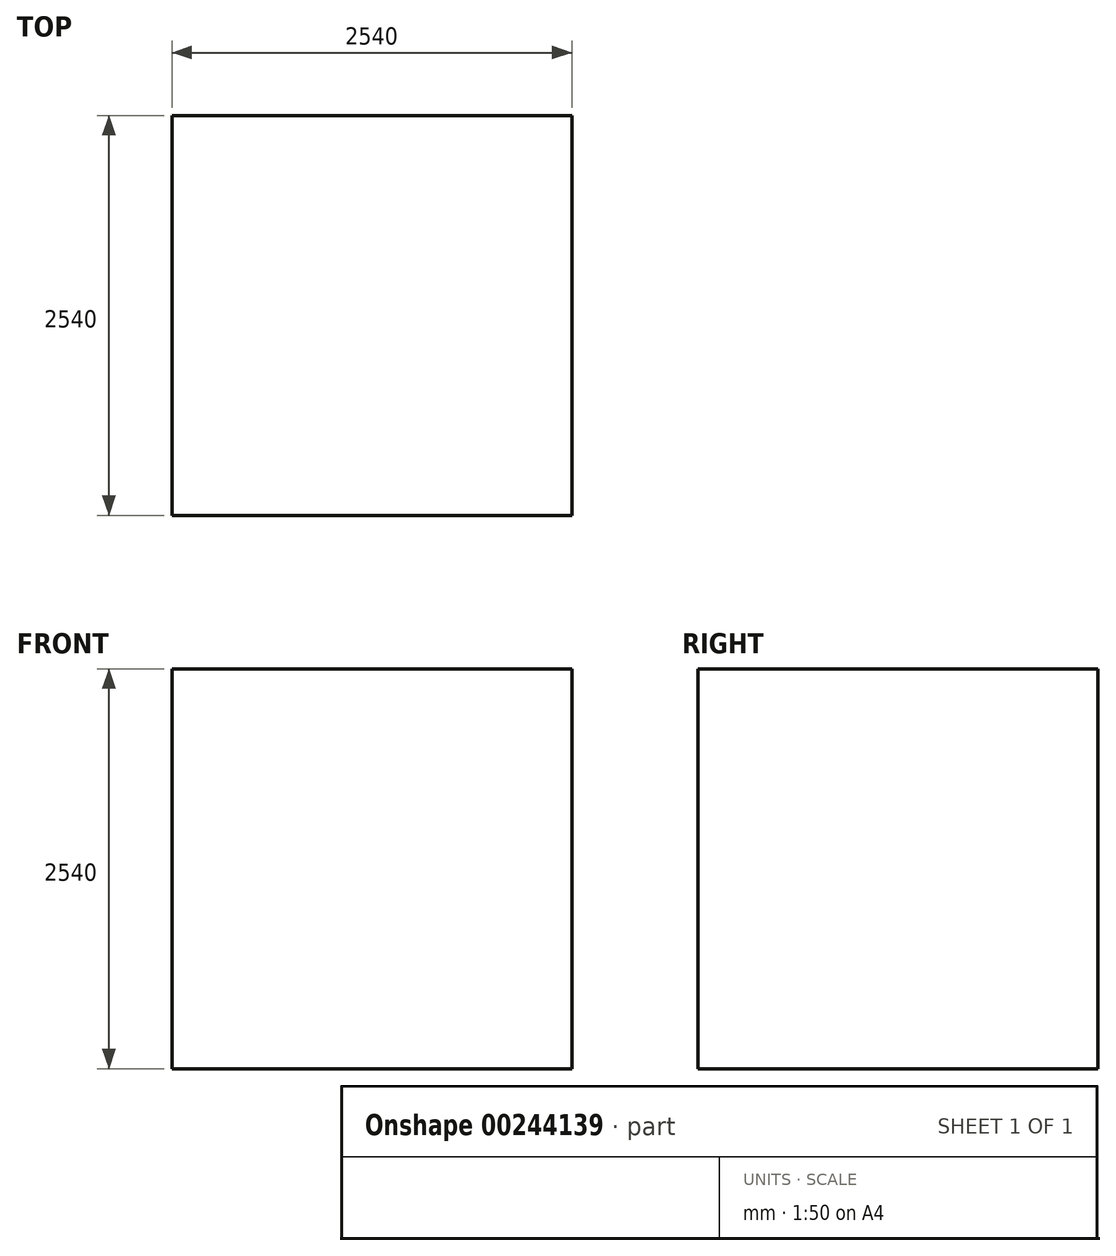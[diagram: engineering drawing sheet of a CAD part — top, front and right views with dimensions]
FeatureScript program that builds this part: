
annotation { "Feature Type Name" : "Feature", "Feature Type Description" : "" }
export const myFeature = defineFeature(function(context is Context, id is Id, definition is map)
    precondition{}
    {
        {
            var Q0;
            Q0=qCreatedBy(makeId("Top.planeOp"),FACE);
            var sketch = newSketch(context, id + "F0", { "sketchPlane" : qUnion([Q0])});
            skLineSegment(sketch, "E0.bottom", {"start": v(-1270.15, 1260.76) * mm, "end": v(1269.85, 1260.76) * mm});
            skLineSegment(sketch, "E0.top", {"start": v(-1270.15, -1279.24) * mm, "end": v(1269.85, -1279.24) * mm});
            skLineSegment(sketch, "E0.left", {"start": v(-1270.15, 1260.76) * mm, "end": v(-1270.15, -1279.24) * mm});
            skLineSegment(sketch, "E0.right", {"start": v(1269.85, 1260.76) * mm, "end": v(1269.85, -1279.24) * mm});
            skSolve(sketch);
        }
        {
            var Q0;
            Q0=makeQuery(id+"F0.imprint","IMPRINT",FACE,{"disambiguationData":[TD([[makeQuery(id+"F0.imprint","IMPRINT",EDGE,{"derivedFrom":sQuery(id+"F0.wireOp",EDGE,"E0.bottom")}),-1.0]])]});
            extrude(context, id + "F1", {"entities" : qUnion([Q0]), "depth" : 2540 * mm});
        }
    });
